# Revit family: LA2 Connected Rings
name_source: partatom
category: Lighting Fixtures
revit_build: Autodesk Revit 2014 (Build: 20130709_2115(x64)
units: mm (PartAtom-declared; Revit-internal decimal feet)

## types (6) — shared parameters
Canopy = La2-connect
Color Filter = 16777215
Comments = This model is for use in spatial massing and rendering. Please contact LightArt for pick-point placement and installation details.
Diffuser = White Opal Acrylic
Dimming Compatibility = 0-10v
Dimming Lamp Color Temperature Shift = <None>
Emit Shape Visible in Rendering = No
Hardware = Stainless Steel Cables
Input = 120v-277v
Length = 4' - 0"
Light Source Symbol Size = 2' - 0"
Manufacturer = LightArt
Model = LA2 Connected Rings
Shade = 3form Varia Ecoresin
Suspension = 4' - 0"

## per-type parameters (varying)
| type | 10' | 12' | 14 | 16 | 6' | 8' | Description | Emit from Circle Diameter | HARDWARE | Height | LIGHTING | STANDARDS | Weight |
| 6'x8"x6" | No | No | No | No | Yes | No | (2)Stainless Steel canopies, 
Mounts to standard junction box | 4' - 0" | (6)3/64” Stainless Steel cables. Adjustable 24”-96” to canopy connection. Custom lengths available. | 1' - 0" | Solid State LED System
120v-277v input; 24v driver;
0-10v dimming compatible
3000k 81 CRI light source
S - 14w, 1050mA, 1045 lumens | 6-8 week lead time, Damp rated, UL Compliant / CSA Approved 
1,000+ 3form material shade options
with fully enclosed acrylic diffuser
CSA Approved to UL standards
Damp Rated
5 year limited warranty | 50 lbs |
| 16'x8"x6" | No | No | No | Yes | No | No | (6) Stainless Steel canopies, 
Mounts to standard junction box | 14' - 0" | (12) 3/64” Stainless Steel cables. Adjustable 24”-96” to canopy connection. Custom lengths available. | 0' - 4" | Solid State LED System
120v-277v input; 24v driver;
0-10v dimming compatible
3000k 81 CRI light source
M - 30w, 2220mA, 2174 lumens | 6-8 week lead time, Damp rated, UL Compliant / CSA Approved | 120 lbs |
| 14'x8"x6" | No | No | Yes | No | No | No | (4) Stainless Steel canopies, 
Mounts to standard junction box | 12' - 0" | (8)3/64” Stainless Steel cables. Adjustable 24”-96” to canopy connection. Custom lengths available. | 1' - 0" | Solid State LED System
120v-277v input; 24v driver;
0-10v dimming compatible
3000k 81 CRI light source
M - 30w, 2220mA, 2174 lumens | 6-8 week lead time, Damp rated, UL Compliant / CSA Approved | 100 lbs |
| 10'x8"x6" | Yes | No | No | No | No | No | (4) Stainless Steel canopies, 
Mounts to standard junction box | 8' - 0" | (8)3/64” Stainless Steel cables. Adjustable 24”-96” to canopy connection. Custom lengths available.
Stainless steel canopy mounts to
standard junction box (provided by others)
(3-4) 3/64” stainless steel cables to canopy
Silver power cord to canopy
Adjustable 24”-96” suspension | 0' - 4" | Solid State LED System
120v-277v input; 24v driver;
0-10v dimming compatible
3000k 81 CRI light source
S - 14w, 1050mA, 1045 lumens | 6-8 week lead time, Damp rated, UL Compliant / CSA Approved | 75 lbs |
| 8'x8"x6" | No | No | No | No | No | Yes | (2) Stainless Steel canopies, 
Mounts to standard junction box | 5' - 0" | (8)3/64” Stainless Steel cables. Adjustable 24”-96” to canopy connection. Custom lengths available. | 0' - 8" | Solid State LED System
120v-277v input; 24v driver;
0-10v dimming compatible
3000k 81 CRI light source
S - 14w, 1050mA, 1045 lumens | 6-8 week lead time, Damp rated, UL Compliant / CSA Approved | 65 lbs |
| 12'x8"x6" | No | Yes | No | No | No | No | (4) Stainless Steel canopies, 
Mounts to standard junction box | 10' - 0" | (8)3/64” Stainless Steel cables. Adjustable 24”-96” to canopy connection. Custom lengths available.
Stainless steel canopy mounts to
standard junction box (provided by others)
(3-4) 3/64” stainless steel cables to canopy
Silver power cord to canopy
Adjustable 24”-96” suspension | 1' - 0" | Solid State LED System
120v-277v input; 24v driver;
0-10v dimming compatible
3000k 81 CRI light source
S - 14w, 1050mA, 1045 lumens | 6-8 week lead time, Damp rated, UL Compliant / CSA Approved | 85 lbs |

## geometry (parser evidence)
native form markers: Blend x2, Sweep x32
no freeform markers — native parametric forms only
